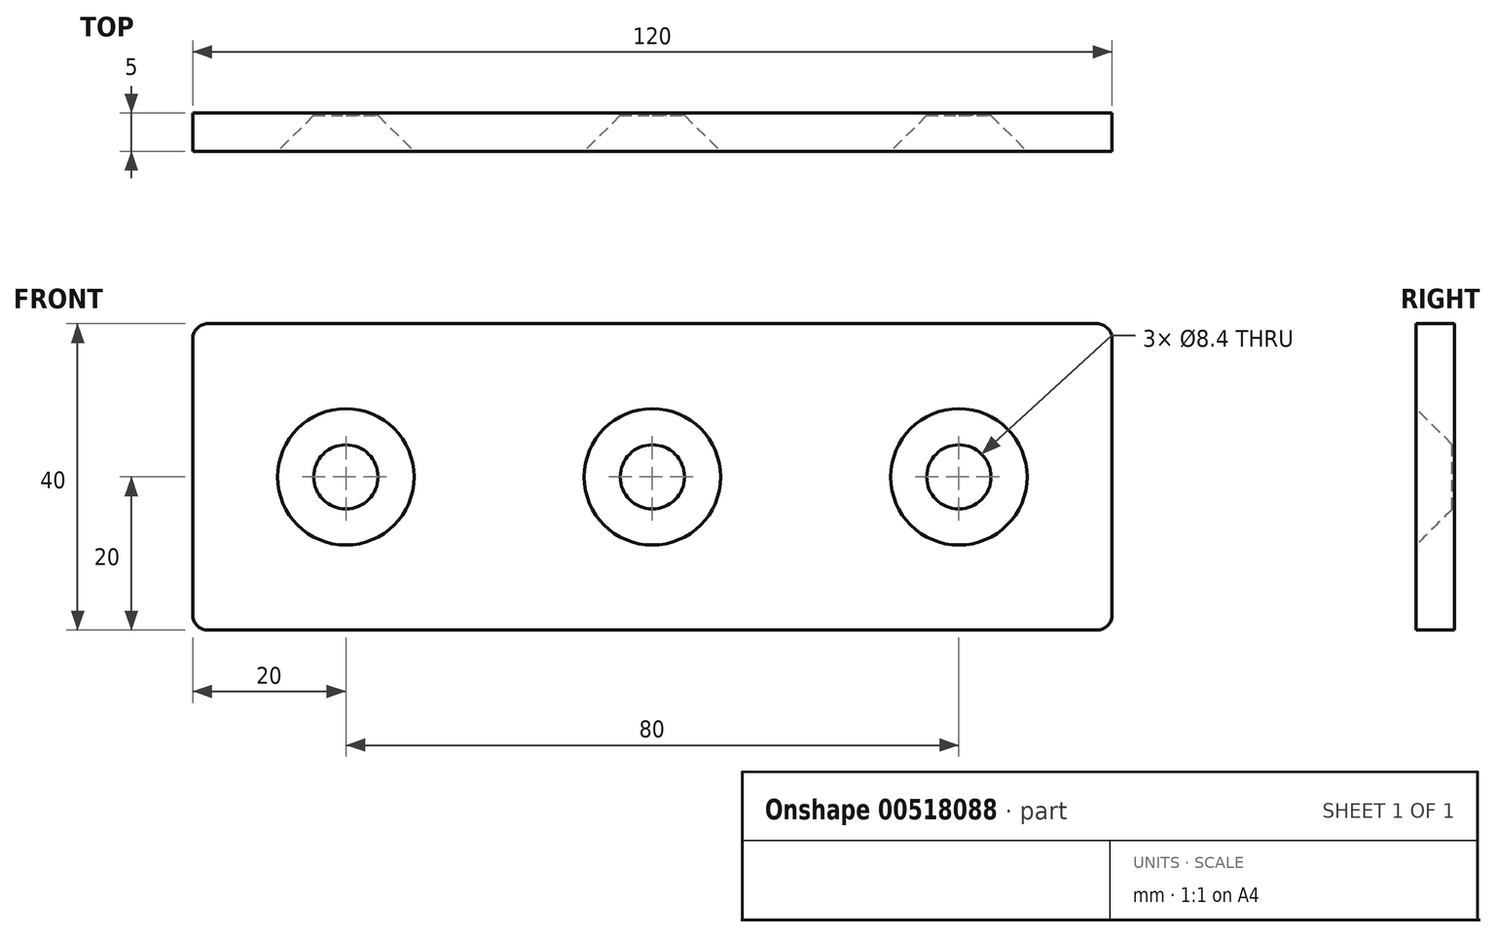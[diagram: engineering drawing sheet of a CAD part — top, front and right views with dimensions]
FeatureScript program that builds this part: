
annotation { "Feature Type Name" : "Feature", "Feature Type Description" : "" }
export const myFeature = defineFeature(function(context is Context, id is Id, definition is map)
    precondition{}
    {
        {
            var Q0;
            Q0=qCreatedBy(makeId("Front.planeOp"),FACE);
            var sketch = newSketch(context, id + "F0", { "sketchPlane" : qUnion([Q0])});
            skCircle(sketch, "E0", {"center": v(0, 0) * mm, "radius": 4.2 * mm});
            skCircle(sketch, "E1.1.0.0", {"center": v(40, 0) * mm, "radius": 4.2 * mm});
            skCircle(sketch, "E1.2.0.0", {"center": v(80, 0) * mm, "radius": 4.2 * mm});
            skLineSegment(sketch, "E1.direction1", {"start": v(0, 0) * mm, "end": v(40, 0) * mm, "construction": true});
            skLineSegment(sketch, "E2.bottom", {"start": v(-18, 20) * mm, "end": v(98, 20) * mm});
            skLineSegment(sketch, "E2.top", {"start": v(-18, -20) * mm, "end": v(98, -20) * mm});
            skLineSegment(sketch, "E2.left", {"start": v(-20, 18) * mm, "end": v(-20, -18) * mm});
            skLineSegment(sketch, "E2.right", {"start": v(100, 18) * mm, "end": v(100, -18) * mm});
            skLineSegment(sketch, "E3", {"start": v(0, 0) * mm, "end": v(-20, 0) * mm, "construction": true});
            skLineSegment(sketch, "E4", {"start": v(80, 0) * mm, "end": v(100, 0) * mm, "construction": true});
            skPoint(sketch, "E5.visualSharp", {"position": v(-20, 20) * mm});
            skArc(sketch, "E5.filletArc", {"start": v(-18, 20) * mm, "mid": v(-19.41, 19.41) * mm, "end": v(-20, 18) * mm});
            skPoint(sketch, "E6.visualSharp", {"position": v(-20, -20) * mm});
            skArc(sketch, "E6.filletArc", {"start": v(-20, -18) * mm, "mid": v(-19.41, -19.41) * mm, "end": v(-18, -20) * mm});
            skPoint(sketch, "E7.visualSharp", {"position": v(100, -20) * mm});
            skArc(sketch, "E7.filletArc", {"start": v(98, -20) * mm, "mid": v(99.41, -19.41) * mm, "end": v(100, -18) * mm});
            skPoint(sketch, "E8.visualSharp", {"position": v(100, 20) * mm});
            skArc(sketch, "E8.filletArc", {"start": v(100, 18) * mm, "mid": v(99.41, 19.41) * mm, "end": v(98, 20) * mm});
            skSolve(sketch);
        }
        {
            var Q0;
            Q0=makeQuery(id+"F0.imprint","IMPRINT",FACE,{"disambiguationData":[TD([[makeQuery(id+"F0.imprint","IMPRINT",EDGE,{"derivedFrom":sQuery(id+"F0.wireOp",EDGE,"E0")}),-1.0]])]});
            extrude(context, id + "F1", {"entities" : qUnion([Q0]), "depth" : 5 * mm, "offsetDistance" : 25 * mm});
        }
        {
            var Q0;
            Q0=makeQuery(id+"F1.opExtrude","CAP_EDGE",EDGE,{"disambiguationData":[OSD([sQuery(id+"F0.wireOp",EDGE,"E0")])],"isStart":false});
            var Q1;
            Q1=makeQuery(id+"F1.opExtrude","CAP_EDGE",EDGE,{"disambiguationData":[OSD([sQuery(id+"F0.wireOp",EDGE,"E1.1.0.0")])],"isStart":false});
            var Q2;
            Q2=makeQuery(id+"F1.opExtrude","CAP_EDGE",EDGE,{"disambiguationData":[OSD([sQuery(id+"F0.wireOp",EDGE,"E1.2.0.0")])],"isStart":false});
            var Q3;
            Q3=makeQuery(id+"F1.opExtrude","CAP_EDGE",EDGE,{"disambiguationData":[OSD([sQuery(id+"F0.wireOp",EDGE,"E1.3.0.0")])],"isStart":false});
            chamfer(context, id + "F2", {"entities" : qUnion([Q0, Q1, Q2, Q3]), "width" : 4.7 * mm, "tangentPropagation" : true});
        }
    });
